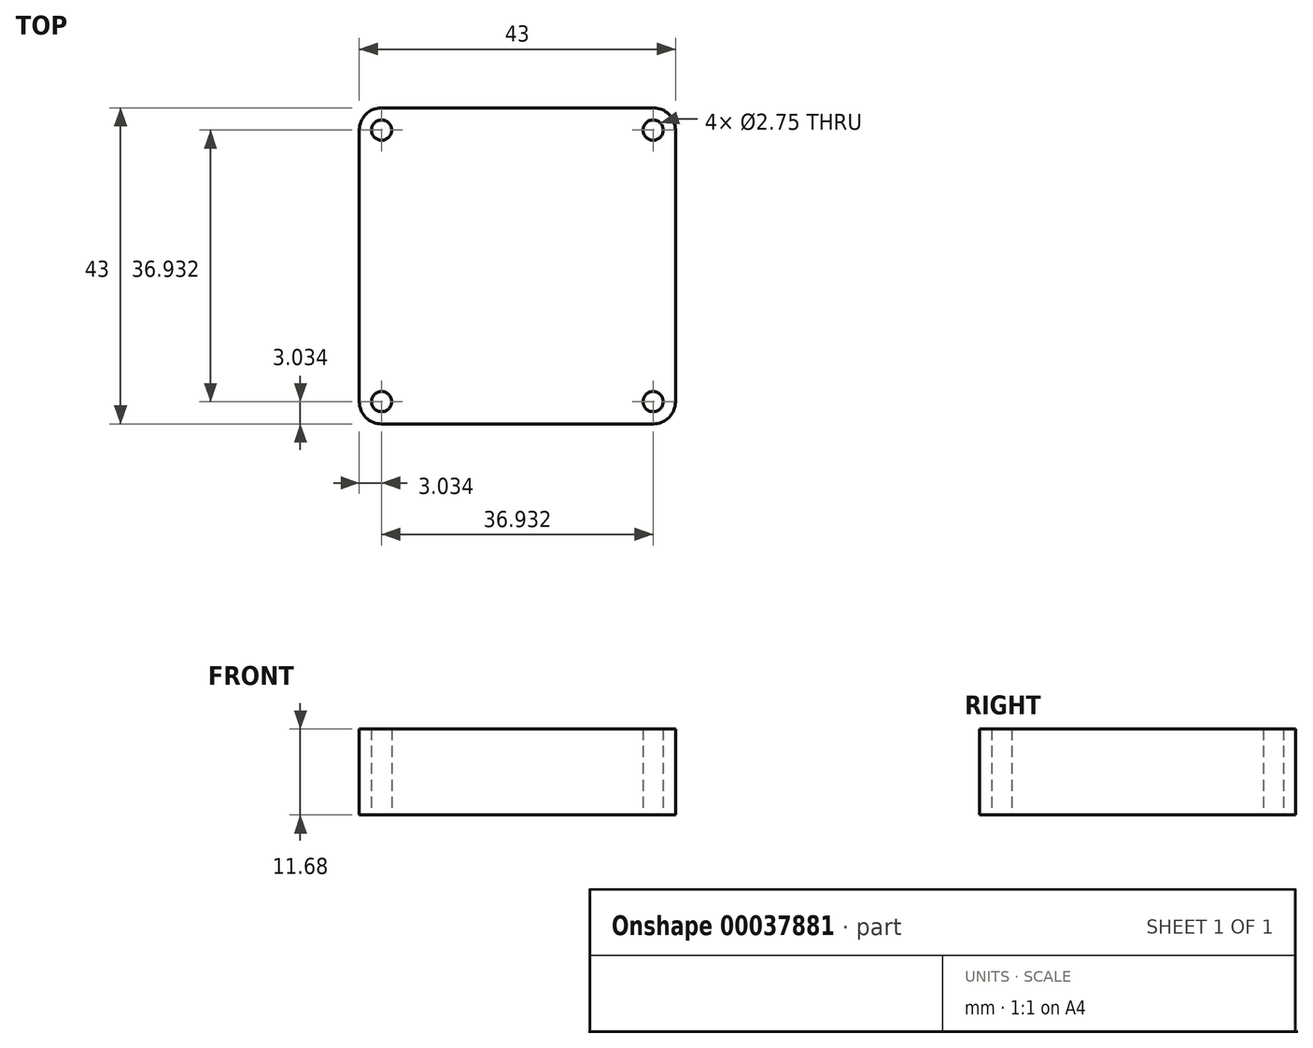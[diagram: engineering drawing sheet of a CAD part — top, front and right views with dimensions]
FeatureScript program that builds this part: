
annotation { "Feature Type Name" : "Feature", "Feature Type Description" : "" }
export const myFeature = defineFeature(function(context is Context, id is Id, definition is map)
    precondition{}
    {
        {
            var Q0;
            Q0=qCreatedBy(makeId("Top.planeOp"),FACE);
            var sketch = newSketch(context, id + "F0", { "sketchPlane" : qUnion([Q0])});
            skLineSegment(sketch, "E0.rect.bottom", {"start": v(21.5, -21.5) * mm, "end": v(-21.5, -21.5) * mm});
            skLineSegment(sketch, "E0.rect.top", {"start": v(21.5, 21.5) * mm, "end": v(-21.5, 21.5) * mm});
            skLineSegment(sketch, "E0.rect.left", {"start": v(21.5, -21.5) * mm, "end": v(21.5, 21.5) * mm});
            skLineSegment(sketch, "E0.rect.right", {"start": v(-21.5, -21.5) * mm, "end": v(-21.5, 21.5) * mm});
            skPoint(sketch, "E0.rect.middle", {"position": v(0, 0) * mm});
            skLineSegment(sketch, "E1.rect.bottom", {"start": v(18.47, -18.47) * mm, "end": v(-18.47, -18.47) * mm, "construction": true});
            skLineSegment(sketch, "E1.rect.top", {"start": v(18.47, 18.47) * mm, "end": v(-18.47, 18.47) * mm, "construction": true});
            skLineSegment(sketch, "E1.rect.left", {"start": v(18.47, -18.47) * mm, "end": v(18.47, 18.47) * mm, "construction": true});
            skLineSegment(sketch, "E1.rect.right", {"start": v(-18.47, -18.47) * mm, "end": v(-18.47, 18.47) * mm, "construction": true});
            skCircle(sketch, "E2", {"center": v(18.47, 18.47) * mm, "radius": 1.37 * mm});
            skCircle(sketch, "E3", {"center": v(18.47, -18.47) * mm, "radius": 1.37 * mm});
            skCircle(sketch, "E4", {"center": v(-18.47, -18.47) * mm, "radius": 1.37 * mm});
            skCircle(sketch, "E5", {"center": v(-18.47, 18.47) * mm, "radius": 1.37 * mm});
            skSolve(sketch);
        }
        {
            var Q0;
            Q0 = qSketchRegion(id + "F0", true);
            extrude(context, id + "F1", {"entities" : qUnion([Q0]), "depth" : 11.68 * mm});
        }
        {
            var Q0;
            Q0=makeQuery(id+"F1.opExtrude","SWEPT_EDGE",EDGE,{"disambiguationData":[OSD([sQuery(id+"F0.wireOp",EDGE,"E0.rect.bottom"),sQuery(id+"F0.wireOp",EDGE,"E0.rect.right")])]});
            var Q1;
            Q1=makeQuery(id+"F1.opExtrude","SWEPT_EDGE",EDGE,{"disambiguationData":[OSD([sQuery(id+"F0.wireOp",EDGE,"E0.rect.bottom"),sQuery(id+"F0.wireOp",EDGE,"E0.rect.left")])]});
            var Q2;
            Q2=makeQuery(id+"F1.opExtrude","SWEPT_EDGE",EDGE,{"disambiguationData":[OSD([sQuery(id+"F0.wireOp",EDGE,"E0.rect.top"),sQuery(id+"F0.wireOp",EDGE,"E0.rect.left")])]});
            var Q3;
            Q3=makeQuery(id+"F1.opExtrude","SWEPT_EDGE",EDGE,{"disambiguationData":[OSD([sQuery(id+"F0.wireOp",EDGE,"E0.rect.top"),sQuery(id+"F0.wireOp",EDGE,"E0.rect.right")])]});
            fillet(context, id + "F2", {"entities" : qUnion([Q0, Q1, Q2, Q3]), "radius" : 3.03 * mm, "tangentPropagation" : true, "allowEdgeOverflow" : false});
        }
    });
